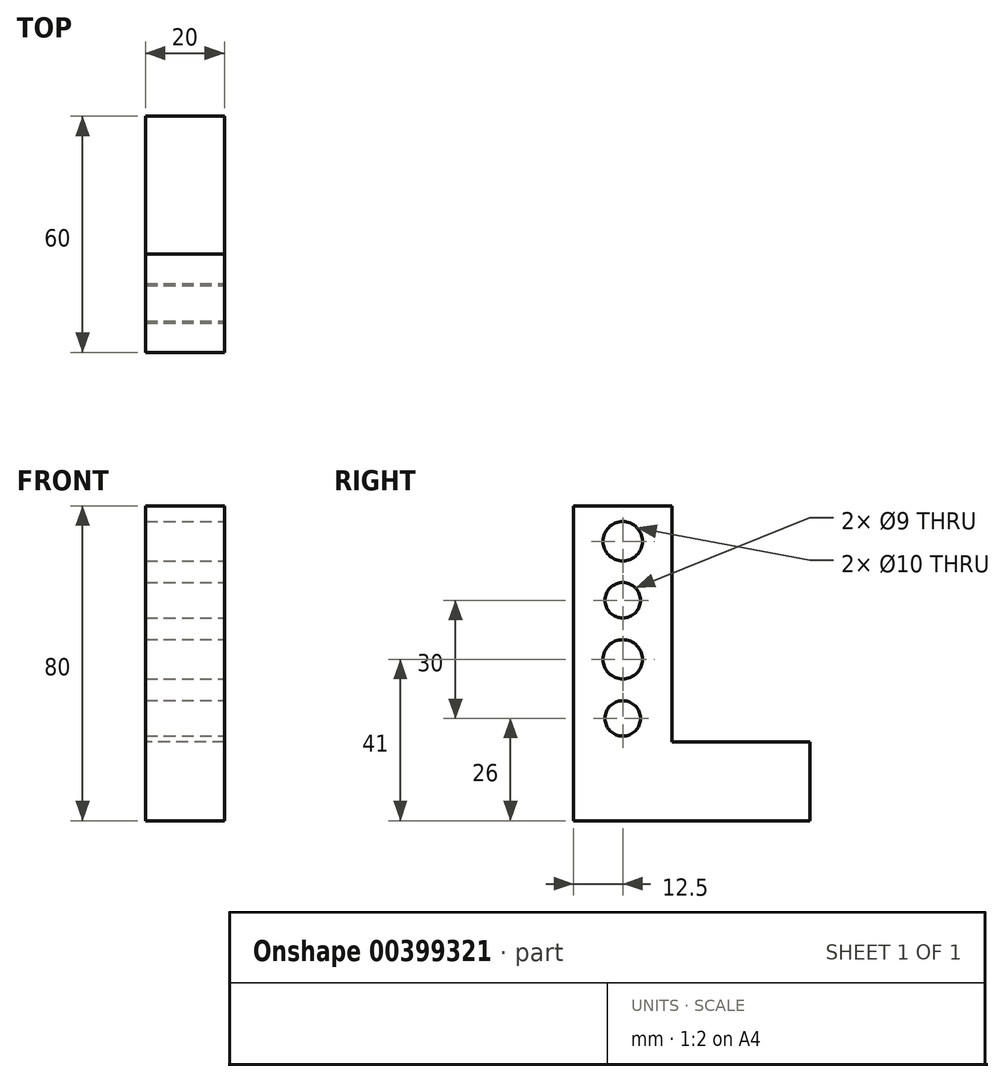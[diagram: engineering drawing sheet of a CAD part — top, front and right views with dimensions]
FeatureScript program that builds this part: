
annotation { "Feature Type Name" : "Feature", "Feature Type Description" : "" }
export const myFeature = defineFeature(function(context is Context, id is Id, definition is map)
    precondition{}
    {
        {
            var Q0;
            Q0=qCreatedBy(makeId("Top.planeOp"),FACE);
            var sketch = newSketch(context, id + "F0", { "sketchPlane" : qUnion([Q0])});
            skLineSegment(sketch, "E0.bottom", {"start": v(0, 0) * mm, "end": v(20, 0) * mm});
            skLineSegment(sketch, "E0.top", {"start": v(0, -25) * mm, "end": v(20, -25) * mm});
            skLineSegment(sketch, "E0.left", {"start": v(0, 0) * mm, "end": v(0, -25) * mm});
            skLineSegment(sketch, "E0.right", {"start": v(20, 0) * mm, "end": v(20, -25) * mm});
            skSolve(sketch);
        }
        {
            var Q0;
            Q0=qSketchRegion(id+"F0",true);
            extrude(context, id + "F1", {"entities" : qUnion([Q0]), "depth" : 80 * mm});
        }
        {
            var Q0;
            Q0=makeQuery(id+"F1.opExtrude","SWEPT_FACE",FACE,{"disambiguationData":[OSD([sQuery(id+"F0.wireOp",EDGE,"E0.right")])]});
            var sketch = newSketch(context, id + "F2", { "sketchPlane" : qUnion([Q0])});
            skLineSegment(sketch, "E1", {"start": v(-12.5, 80) * mm, "end": v(-12.5, 71) * mm, "construction": true});
            skPoint(sketch, "E1.endSnap0", {"position": v(-12.5, 80) * mm});
            skLineSegment(sketch, "E2", {"start": v(-12.5, 71) * mm, "end": v(-12.5, 56) * mm, "construction": true});
            skLineSegment(sketch, "E3", {"start": v(-12.5, 56) * mm, "end": v(-12.5, 41) * mm, "construction": true});
            skLineSegment(sketch, "E4", {"start": v(-12.5, 41) * mm, "end": v(-12.5, 26) * mm, "construction": true});
            skLineSegment(sketch, "E5", {"start": v(-12.5, 26) * mm, "end": v(-12.5, 0) * mm, "construction": true});
            skCircle(sketch, "E6", {"center": v(-12.5, 71) * mm, "radius": 5 * mm});
            skCircle(sketch, "E7", {"center": v(-12.5, 56) * mm, "radius": 4.5 * mm});
            skCircle(sketch, "E8", {"center": v(-12.5, 41) * mm, "radius": 5 * mm});
            skCircle(sketch, "E9", {"center": v(-12.5, 26) * mm, "radius": 4.5 * mm});
            skSolve(sketch);
        }
        {
            var Q0;
            Q0=qSketchRegion(id+"F2",true);
            extrude(context, id + "F3", {"entities" : qUnion([Q0]), "operationType" : NewBodyOperationType.REMOVE, "oppositeDirection" : true, "depth" : 25 * mm});
        }
        {
            var Q0;
            Q0=makeQuery(id+"F1.opExtrude","SWEPT_FACE",FACE,{"disambiguationData":[OSD([sQuery(id+"F0.wireOp",EDGE,"E0.bottom")])]});
            var sketch = newSketch(context, id + "F4", { "sketchPlane" : qUnion([Q0])});
            skLineSegment(sketch, "E10.bottom", {"start": v(-20, 0) * mm, "end": v(0, 0) * mm});
            skLineSegment(sketch, "E10.top", {"start": v(-20, 20) * mm, "end": v(0, 20) * mm});
            skLineSegment(sketch, "E10.left", {"start": v(-20, 0) * mm, "end": v(-20, 20) * mm});
            skLineSegment(sketch, "E10.right", {"start": v(0, 0) * mm, "end": v(0, 20) * mm});
            skSolve(sketch);
        }
        {
            var Q0;
            Q0=qSketchRegion(id+"F4",true);
            extrude(context, id + "F5", {"entities" : qUnion([Q0]), "operationType" : NewBodyOperationType.ADD, "depth" : 35 * mm});
        }
    });
